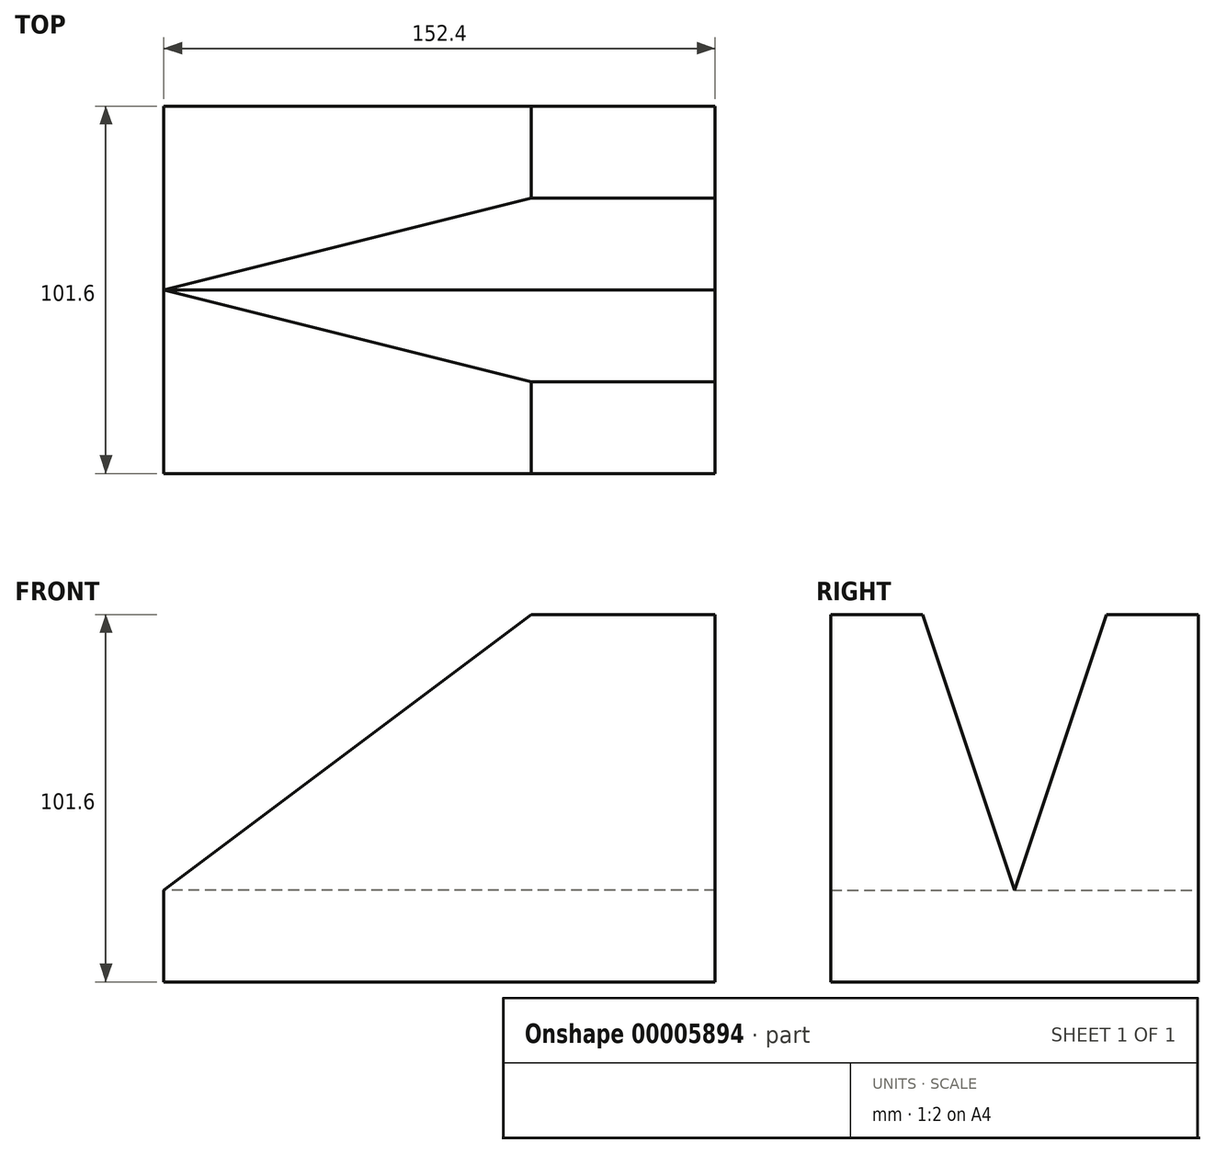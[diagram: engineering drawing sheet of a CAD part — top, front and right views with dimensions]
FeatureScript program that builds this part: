
annotation { "Feature Type Name" : "Feature", "Feature Type Description" : "" }
export const myFeature = defineFeature(function(context is Context, id is Id, definition is map)
    precondition{}
    {
        {
            var Q0;
            Q0=qCreatedBy(makeId("Front.planeOp"),FACE);
            var sketch = newSketch(context, id + "F0", { "sketchPlane" : qUnion([Q0])});
            skLineSegment(sketch, "E0", {"start": v(0, 0) * mm, "end": v(152.4, 0) * mm});
            skLineSegment(sketch, "E1", {"start": v(152.4, 0) * mm, "end": v(152.4, 101.6) * mm});
            skLineSegment(sketch, "E2", {"start": v(152.4, 101.6) * mm, "end": v(101.6, 101.6) * mm});
            skLineSegment(sketch, "E3", {"start": v(101.6, 101.6) * mm, "end": v(0, 25.4) * mm});
            skLineSegment(sketch, "E4", {"start": v(0, 25.4) * mm, "end": v(0, 0) * mm});
            skSolve(sketch);
        }
        {
            var Q0;
            Q0=makeQuery(id+"F0.imprint","IMPRINT",FACE,{"disambiguationData":[TD([[makeQuery(id+"F0.imprint","IMPRINT",EDGE,{"derivedFrom":sQuery(id+"F0.wireOp",EDGE,"E0")}),1.0]])]});
            extrude(context, id + "F1", {"entities" : qUnion([Q0]), "depth" : 50.8 * mm});
        }
        {
            var Q0;
            Q0=makeQuery(id+"F1.opExtrude","SWEPT_FACE",FACE,{"disambiguationData":[OSD([sQuery(id+"F0.wireOp",EDGE,"E2")])]});
            var sketch = newSketch(context, id + "F2", { "sketchPlane" : qUnion([Q0])});
            skLineSegment(sketch, "E5", {"start": v(0, 0) * mm, "end": v(101.6, -25.4) * mm});
            skLineSegment(sketch, "E6", {"start": v(101.6, -25.4) * mm, "end": v(152.4, -25.4) * mm});
            skLineSegment(sketch, "E7", {"start": v(152.4, -25.4) * mm, "end": v(152.4, 0) * mm});
            skLineSegment(sketch, "E8", {"start": v(152.4, 0) * mm, "end": v(0, 0) * mm});
            skSolve(sketch);
        }
        {
            var Q0;
            {var subQ1=sQuery(id+"F2.wireOp",EDGE,"E6");Q0=makeQuery(id+"F2.imprint","IMPRINT",FACE,{"disambiguationData":[TD([[makeQuery(id+"F2.imprint","IMPRINT",EDGE,{"derivedFrom":subQ1}),1.0]])]});}
            var Q1;
            {var subQ1=sQuery(id+"F2.wireOp",EDGE,"E5");Q1=makeQuery(id+"F2.imprint","IMPRINT",FACE,{"disambiguationData":[TD([[makeQuery(id+"F2.imprint","IMPRINT",EDGE,{"derivedFrom":subQ1}),1.0]])]});}
            extrude(context, id + "F3", {"entities" : qUnion([Q0, Q1]), "operationType" : NewBodyOperationType.REMOVE, "oppositeDirection" : true, "depth" : 76.2 * mm});
        }
        {
            var Q0;
            Q0=makeQuery(id+"F1.opExtrude","SWEPT_FACE",FACE,{"disambiguationData":[OSD([sQuery(id+"F0.wireOp",EDGE,"E1")])]});
            var sketch = newSketch(context, id + "F4", { "sketchPlane" : qUnion([Q0])});
            skLineSegment(sketch, "E9", {"start": v(0, 25.4) * mm, "end": v(-25.4, 101.6) * mm});
            skLineSegment(sketch, "E10", {"start": v(-25.4, 101.6) * mm, "end": v(-25.4, 25.4) * mm});
            skLineSegment(sketch, "E11", {"start": v(-25.4, 25.4) * mm, "end": v(0, 25.4) * mm});
            skSolve(sketch);
        }
        {
            var Q0;
            Q0=makeQuery(id+"F4.imprint","IMPRINT",FACE,{"disambiguationData":[TD([[makeQuery(id+"F4.imprint","IMPRINT",EDGE,{"derivedFrom":sQuery(id+"F4.wireOp",EDGE,"E9")}),1.0]])]});
            extrude(context, id + "F5", {"entities" : qUnion([Q0]), "operationType" : NewBodyOperationType.ADD, "oppositeDirection" : true, "depth" : 152.4 * mm});
        }
        {
            var Q0;
            Q0=makeQuery(id+"F5.opExtrude","SWEPT_FACE",FACE,{"disambiguationData":[OSD([sQuery(id+"F4.wireOp",EDGE,"E10")])]});
            var sketch = newSketch(context, id + "F6", { "sketchPlane" : qUnion([Q0])});
            skSolve(sketch);
        }
        {
            var Q0;
            {var subQ0=sQuery(id+"F4.wireOp",EDGE,"E10");Q0=makeQuery(id+"F6.imprint","IMPRINT",FACE,{"disambiguationData":[TD([[makeQuery(id+"F6.imprint","IMPRINT",EDGE,{"derivedFrom":makeQuery(id+"F5.opExtrude","CAP_EDGE",EDGE,{"disambiguationData":[OSD([subQ0])],"isStart":false})}),-1.0]])]});}
            extrude(context, id + "F7", {"entities" : qUnion([Q0]), "operationType" : NewBodyOperationType.REMOVE, "oppositeDirection" : true, "depth" : 25.4 * mm});
        }
        {
            var Q0;
            Q0=makeQuery(id+"F1.opExtrude","CAP_FACE",FACE,{"disambiguationData":[OSD([sQuery(id+"F0.wireOp",EDGE,"E0"),sQuery(id+"F0.wireOp",EDGE,"E1"),sQuery(id+"F0.wireOp",EDGE,"E2"),sQuery(id+"F0.wireOp",EDGE,"E3"),sQuery(id+"F0.wireOp",EDGE,"E4")])],"isStart":true});
            extrude(context, id + "F8", {"entities" : qUnion([Q0]), "operationType" : NewBodyOperationType.ADD, "depth" : 50.8 * mm});
        }
        {
            var Q0;
            {var subQ0=sQuery(id+"F0.wireOp",EDGE,"E1");Q0=makeQuery(id+"F8.boolean.opBoolean","MERGE",FACE,{"derivedFrom":[makeQuery(id+"F5.boolean.opBoolean","MERGE",FACE,{"derivedFrom":[makeQuery(id+"F1.opExtrude","SWEPT_FACE",FACE,{"disambiguationData":[OSD([subQ0])]}),makeQuery(id+"F5.opExtrude","CAP_FACE",FACE,{"disambiguationData":[OSD([sQuery(id+"F4.wireOp",EDGE,"E9"),sQuery(id+"F4.wireOp",EDGE,"E10"),sQuery(id+"F4.wireOp",EDGE,"E11")])],"isStart":true})]}),makeQuery(id+"F8.opExtrude","SWEPT_FACE",FACE,{"disambiguationData":[OSD([subQ0])]})]});}
            var sketch = newSketch(context, id + "F9", { "sketchPlane" : qUnion([Q0])});
            skLineSegment(sketch, "E12", {"start": v(50.8, 25.4) * mm, "end": v(50.8, 101.6) * mm});
            skLineSegment(sketch, "E13", {"start": v(50.8, 101.6) * mm, "end": v(25.4, 101.6) * mm});
            skLineSegment(sketch, "E14", {"start": v(25.4, 101.6) * mm, "end": v(0, 25.4) * mm});
            skSolve(sketch);
        }
        {
            var Q0;
            Q0=makeQuery(id+"F9.imprint","IMPRINT",FACE,{"disambiguationData":[TD([[makeQuery(id+"F9.imprint","IMPRINT",EDGE,{"derivedFrom":sQuery(id+"F9.wireOp",EDGE,"E12")}),1.0]])]});
            extrude(context, id + "F10", {"entities" : qUnion([Q0]), "operationType" : NewBodyOperationType.ADD, "oppositeDirection" : true, "depth" : 152.4 * mm});
        }
        {
            var Q0;
            Q0=makeQuery(id+"F10.boolean.opBoolean","MERGE",FACE,{"derivedFrom":[makeQuery(id+"F8.opExtrude","CAP_FACE",FACE,{"disambiguationData":[OSD([sQuery(id+"F0.wireOp",EDGE,"E0"),sQuery(id+"F0.wireOp",EDGE,"E1"),sQuery(id+"F0.wireOp",EDGE,"E2"),sQuery(id+"F0.wireOp",EDGE,"E3"),sQuery(id+"F0.wireOp",EDGE,"E4")])],"isStart":false}),makeQuery(id+"F10.opExtrude","SWEPT_FACE",FACE,{"disambiguationData":[OSD([sQuery(id+"F9.wireOp",EDGE,"E12")])]})]});
            var sketch = newSketch(context, id + "F11", { "sketchPlane" : qUnion([Q0])});
            skLineSegment(sketch, "E15", {"start": v(0, 101.6) * mm, "end": v(-101.6, 101.6) * mm});
            skLineSegment(sketch, "E16", {"start": v(-101.6, 101.6) * mm, "end": v(0, 25.4) * mm});
            skLineSegment(sketch, "E17", {"start": v(0, 25.4) * mm, "end": v(0, 101.6) * mm});
            skSolve(sketch);
        }
        {
            var Q0;
            Q0=makeQuery(id+"F11.imprint","IMPRINT",FACE,{"disambiguationData":[TD([[makeQuery(id+"F11.imprint","IMPRINT",EDGE,{"derivedFrom":sQuery(id+"F11.wireOp",EDGE,"E15")}),1.0]])]});
            extrude(context, id + "F12", {"entities" : qUnion([Q0]), "operationType" : NewBodyOperationType.REMOVE, "oppositeDirection" : true, "depth" : 50.8 * mm});
        }
    });
